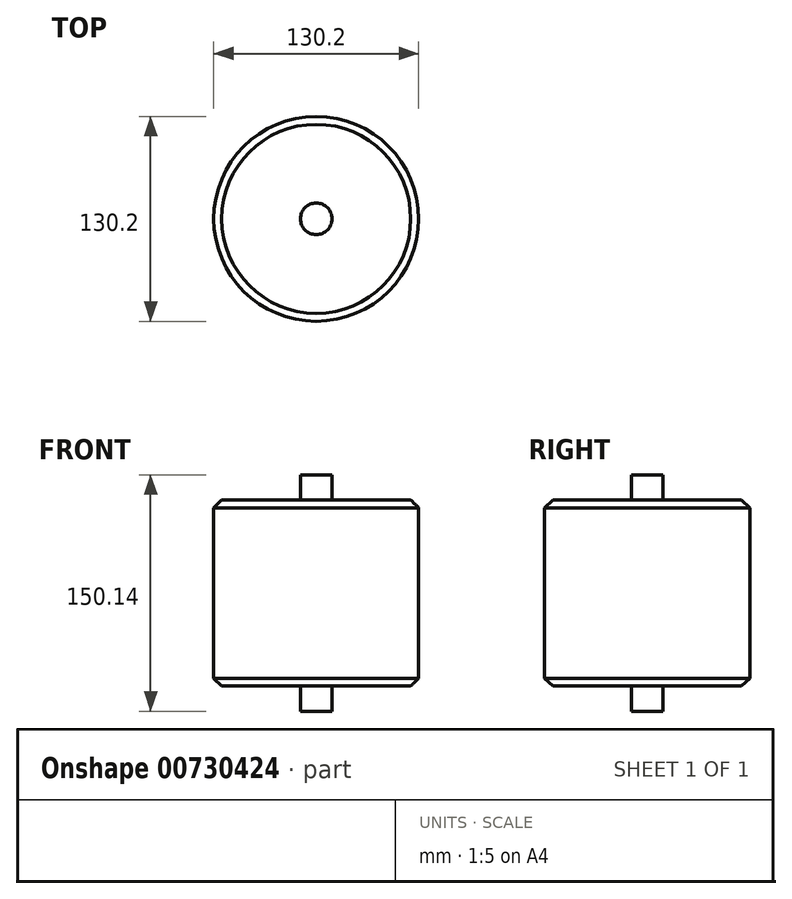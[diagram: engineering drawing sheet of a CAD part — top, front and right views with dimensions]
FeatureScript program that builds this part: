
annotation { "Feature Type Name" : "Feature", "Feature Type Description" : "" }
export const myFeature = defineFeature(function(context is Context, id is Id, definition is map)
    precondition{}
    {
        {
            var Q0;
            Q0=qCreatedBy(makeId("Front.planeOp"),FACE);
            var sketch = newSketch(context, id + "F0", { "sketchPlane" : qUnion([Q0])});
            skLineSegment(sketch, "E0", {"start": v(0, 75.2) * mm, "end": v(10, 75.2) * mm});
            skLineSegment(sketch, "E1", {"start": v(10, 75.2) * mm, "end": v(10, 59.2) * mm});
            skLineSegment(sketch, "E2", {"start": v(10, 59.2) * mm, "end": v(60, 59.2) * mm});
            skLineSegment(sketch, "E3", {"start": v(60, 59.2) * mm, "end": v(65.1, 54.25) * mm});
            skLineSegment(sketch, "E4", {"start": v(0, -74.93) * mm, "end": v(10, -74.93) * mm});
            skLineSegment(sketch, "E5", {"start": v(10, -74.93) * mm, "end": v(10, -58.93) * mm});
            skLineSegment(sketch, "E6", {"start": v(10, -58.93) * mm, "end": v(60, -58.93) * mm});
            skLineSegment(sketch, "E7", {"start": v(65.1, 54.25) * mm, "end": v(65.1, -53.96) * mm});
            skLineSegment(sketch, "E8", {"start": v(65.1, -53.96) * mm, "end": v(60, -58.93) * mm});
            skLineSegment(sketch, "E9", {"start": v(0, 75.2) * mm, "end": v(0, -74.93) * mm});
            skSolve(sketch);
        }
        {
            var Q0;
            Q0=makeQuery(id+"F0.imprint","IMPRINT",FACE,{"disambiguationData":[TD([[makeQuery(id+"F0.imprint","IMPRINT",EDGE,{"derivedFrom":sQuery(id+"F0.wireOp",EDGE,"E0")}),-1.0]])]});
            var Q1;
            Q1=sQuery(id+"F0.wireOp",EDGE,"E9");
            revolve(context, id + "F1", {"surfaceOperationType" : NewSurfaceOperationType.NEW, "entities" : qUnion([Q0]), "axis" : qUnion([Q1]), "revolveType" : RevolveType.FULL});
        }
    });
